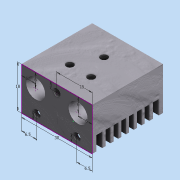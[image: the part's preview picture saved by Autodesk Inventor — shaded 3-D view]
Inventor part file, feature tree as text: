
AUTODESK INVENTOR PART (.ipt)
format: ipt  version: 2016 (Build 200138000, 138)  size: 225,792 bytes
history: native  units: mm
features: thread x6, hole x4, sketch x3, extrude x2
ambient origin geometry x8: Origin, YZ Plane, XZ Plane, XY Plane, X Axis, Y Axis, Z Axis, Center Point
bodies: Solid1 (feature_tree)
feature tree (15):
  sketch  "Sketch2"  dims[d0=30.0mm d1=18.0mm]
  extrude  "Extrusion1"  Depth=18.0mm
  hole  "Hole1"  [1 undecoded]
  hole  "Hole2"  [1 undecoded]
  extrude  "Extrusion3"  Depth=10.0mm TaperAngle=0.0deg
  hole  "Hole3"  [1 undecoded]
  thread  "Thread1"  [1 undecoded]
  thread  "Thread2"  [1 undecoded]
  thread  "Thread3"  [1 undecoded]
  hole  "Hole4"  [1 undecoded]
  thread  "Thread4"  [1 undecoded]
  thread  "Thread5"  [1 undecoded]
  thread  "Thread6"  [1 undecoded]
  sketch  "Sketch3"  dims[d2=6.0mm d3=6.0mm]
  sketch  "Sketch4"  dims[d4=6.0mm d5=6.0mm d6=30.0mm d7=0.0mm d8=7.0mm d9=6.0mm d10=4.0mm d11=2.0mm d12=90.0deg d13=8.0mm d14=20.594885mm d15=8.0mm d16=6.0mm d17=4.0mm d18=2.0mm d19=90.0deg d20=6.5mm d21=20.594885mm d22=6.0mm d23=2.5mm d24=1.75mm d25=6.0mm d26=2.0mm d27=1.5mm d36=6.0mm d37=2.5mm d40=15.0mm d41=3.0mm d42=6.5mm d43=6.5mm d44=3.0mm d45=3.0mm d46=6.0mm d47=2.0mm d48=1.3mm d49=6.0mm d50=2.0mm d51=6.0mm d52=2.0mm d53=6.0mm d54=2.0mm d55=6.0mm d56=2.0mm d57=1.75mm d58=1.5mm d59=30.0mm d60=0.0mm d61=3.0mm d62=6.0mm d63=4.0mm d64=2.0mm d65=90.0deg d66=10.0mm d67=0.0mm d68=10.0mm d69=0.0mm d70=10.0mm d71=0.0mm d72=10.0mm d73=0.0mm d74=10.5mm d75=15.0mm d76=19.5mm d77=20.0mm d78=10.0mm d79=3.0mm d80=6.0mm d81=4.0mm d82=2.0mm d83=90.0deg d84=10.0mm d85=0.0mm d86=10.0mm d87=0.0mm d88=10.0mm d89=0.0mm d90=10.0mm d91=0.0mm]
note: 10 required parameter values undecoded (feature->parameter linkage not recoverable at this tier; creation-order binding heuristic only, values carry confidence <= 0.55)
